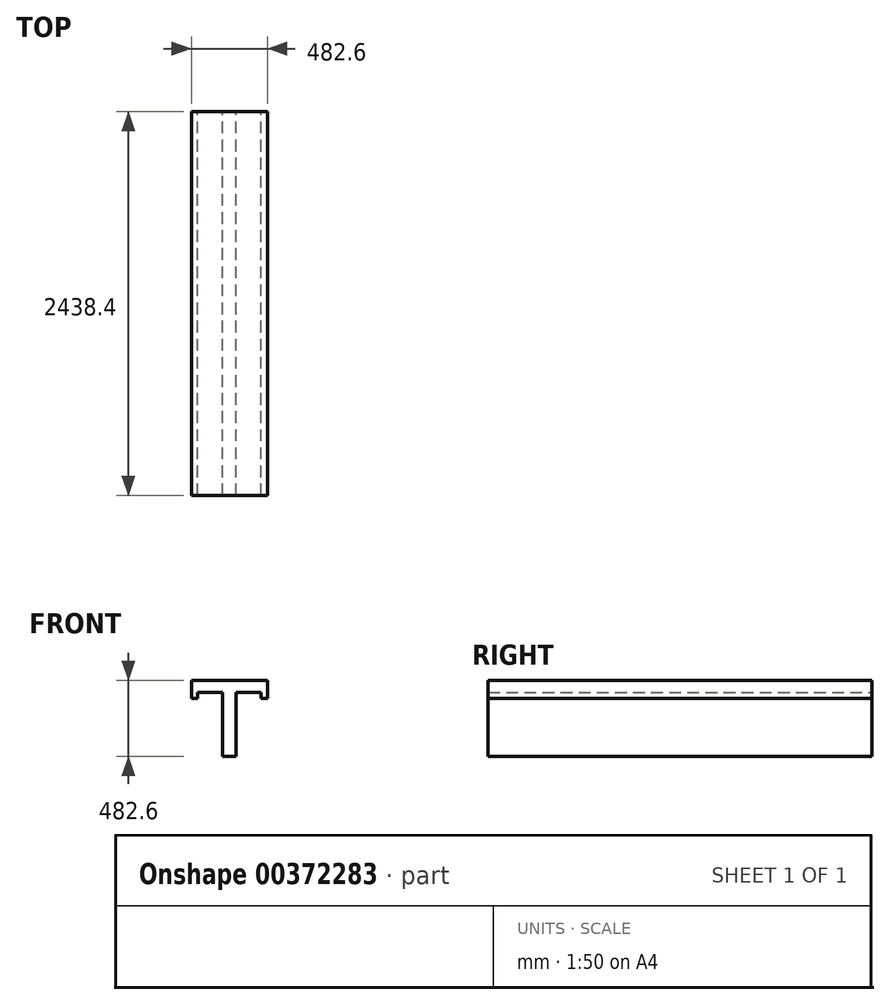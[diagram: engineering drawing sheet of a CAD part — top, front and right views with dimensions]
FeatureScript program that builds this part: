
annotation { "Feature Type Name" : "Feature", "Feature Type Description" : "" }
export const myFeature = defineFeature(function(context is Context, id is Id, definition is map)
    precondition{}
    {
        {
            var Q0;
            Q0=qCreatedBy(makeId("Front.planeOp"),FACE);
            var sketch = newSketch(context, id + "F0", { "sketchPlane" : qUnion([Q0])});
            skLineSegment(sketch, "E0", {"start": v(0, 0) * mm, "end": v(44.45, 0) * mm});
            skLineSegment(sketch, "E1", {"start": v(44.45, 0) * mm, "end": v(44.45, 406.4) * mm});
            skLineSegment(sketch, "E2", {"start": v(44.45, 406.4) * mm, "end": v(203.2, 406.4) * mm});
            skLineSegment(sketch, "E3", {"start": v(203.2, 406.4) * mm, "end": v(203.2, 368.3) * mm});
            skLineSegment(sketch, "E4", {"start": v(203.2, 368.3) * mm, "end": v(241.3, 368.3) * mm});
            skLineSegment(sketch, "E5", {"start": v(241.3, 368.3) * mm, "end": v(241.3, 482.6) * mm});
            skLineSegment(sketch, "E6", {"start": v(241.3, 482.6) * mm, "end": v(0, 482.6) * mm});
            skLineSegment(sketch, "E7", {"start": v(0, 238.98) * mm, "end": v(0, -198.83) * mm, "construction": true});
            skLineSegment(sketch, "E8.MirrorCS", {"start": v(-44.45, 0) * mm, "end": v(-44.45, 406.4) * mm});
            skLineSegment(sketch, "E9.MirrorCS", {"start": v(-44.45, 406.4) * mm, "end": v(-203.2, 406.4) * mm});
            skLineSegment(sketch, "E10.MirrorCS", {"start": v(-203.2, 368.3) * mm, "end": v(-241.3, 368.3) * mm});
            skLineSegment(sketch, "E11.MirrorCS", {"start": v(-203.2, 406.4) * mm, "end": v(-203.2, 368.3) * mm});
            skLineSegment(sketch, "E12.MirrorCS", {"start": v(-241.3, 368.3) * mm, "end": v(-241.3, 482.6) * mm});
            skLineSegment(sketch, "E13.MirrorCS", {"start": v(-241.3, 482.6) * mm, "end": v(0, 482.6) * mm});
            skLineSegment(sketch, "E14.MirrorCS", {"start": v(0, 0) * mm, "end": v(-44.45, 0) * mm});
            skSolve(sketch);
        }
        {
            var Q0;
            Q0 = qSketchRegion(id + "F0", true);
            extrude(context, id + "F1", {"entities" : qUnion([Q0]), "depth" : 2438.4 * mm});
        }
    });
